# Revit family: Loudspeaker-Ceiling Mounted-Q-SYS-AD-C6T-ZB
name_source: partatom
category: Communication Devices
units: mm (PartAtom-declared; Revit-internal decimal feet)

## family parameters
Cut with Voids When Loaded = No
Host = Face
Maintain Annotation Orientation = No
OmniClass Number = 23.85.10.11.14.14.14
OmniClass Title = Loudspeakers
Part Type = Normal
Room Calculation Point = No
Round Connector Dimension = Use Diameter
Shared = No

## types (1)
- White
    100V Taps = 15 W, 30 W, 60 W
    70V Taps = 3.75 W, 7.5 W, 15 W, 30 W
    ATB Inside Diameter = 10 "
    ATB Inside Radius = 5 "
    Assembly Code = E1020500
    Body Diameter = 9.53 "
    Body Height = 8.69 "
    Body Material = Paint - Q-SYS - Black
    Body Radius = 4.77 "
    Clip Diameter = 0.3 "
    Clip Height = 0.4 "
    Clip Radius = 0.15 "
    Cover Material = Paint - Q-SYS - White
    Cover Radius = 5.52 "
    Coverage Horizontal = 135.00°
    Coverage Vertical = 135.00°
    Default Elevation = 48 "
    Description = 6.5” small format, zero bezel ceiling mount loudspeaker.
    Frequency Range = 70 Hz - 20 kHz
    Grille Diameter = 11.03 "
    Grille Height = 0.2 "
    Grille Radius = 5.52 "
    Highlight Material = Fabric - Q-SYS - White Mesh
    IQ Category = Loudspeaker
    Impedance = 16
    Length 1 = 4.52 "
    Length 10 = 1 "
    Length 11 = 0.58 "
    Length 15 = 5.75 "
    Length 2 = 6.43 "
    Length 4 = 5.8 "
    Length 7 = 1 "
    Length 8 = 0.77 "
    Length 9 = 0.59 "
    Manufacturer = Q-SYS
    Manufacturer URL = https://www.qsys.com
    Model = AD-C6T-ZB
    Number of Bands = 1
    Offset = 0 "
    OmniClass Number = 23.85.10.11.14.14.14
    Part Number = AD-C6T-ZB
    Product Documentation Link = https://www.qsys.com
    Product Page URL = https://www.qsys.com
    Rail Width = 0.88 "
    Regulatory Compliance = UL1480, UL2043, NFPA90, NFPA70 suitable for use in air handling spaces. Transformer UL registered per UL1876, ROHS, CE compliant. Baffle meets UL94-V0 and UL94-5 VB flamibility rating; in accordance with IEC60849 / EN60849 systems.
    SPL Max = 106
    Sensitivity = 88
    Support Length = 25.57 "
    Support Material = Metal - Q-SYS - Steel
    Support Width = 25.3 "
    Taper Angle = 3.00°
    Type Comments = White
    URL = https://www.qsys.com
    Weight = 9.50 lbm
    Weight Dimensional = 27.8
    Weight Product = 9.5
    Width = 11.03 "

## geometry (parser evidence)
native form markers: Sweep x5
no freeform markers — native parametric forms only
